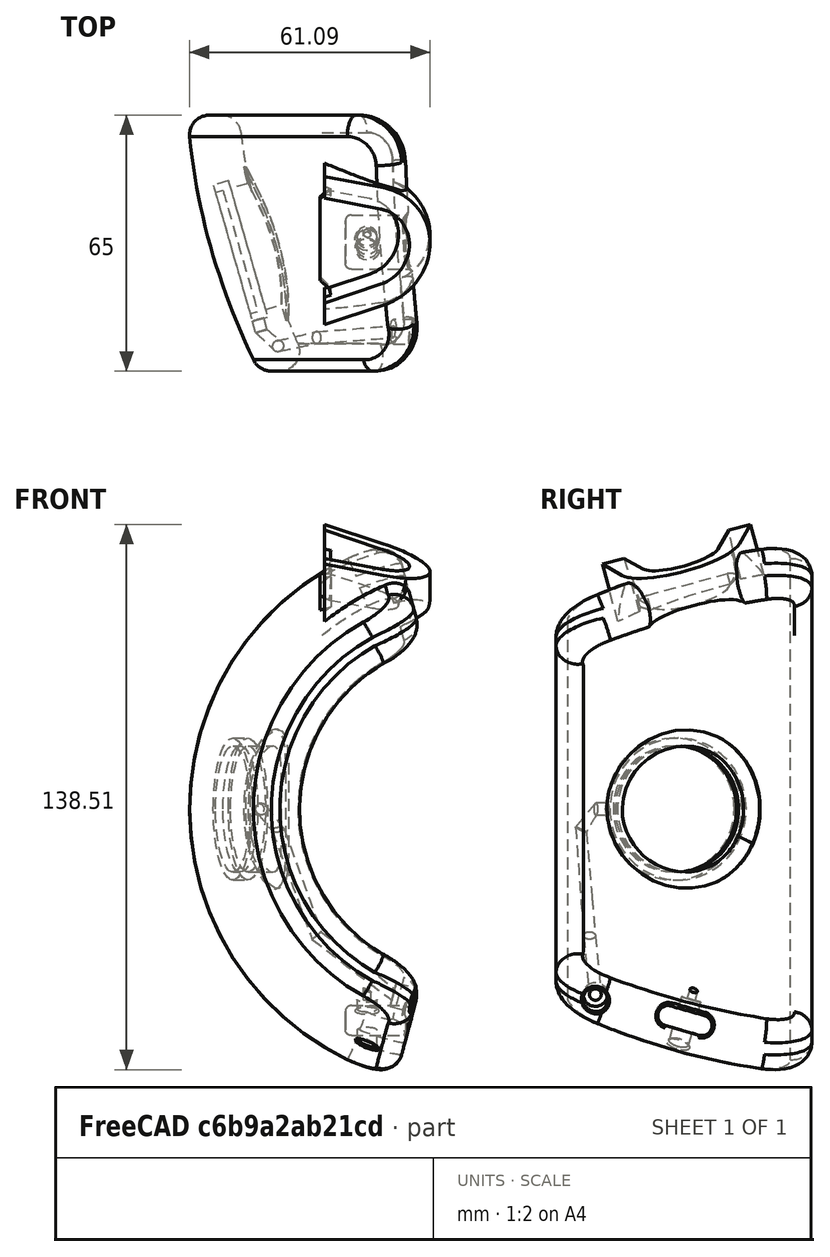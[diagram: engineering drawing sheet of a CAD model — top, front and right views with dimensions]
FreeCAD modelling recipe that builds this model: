
FCSTD DOCUMENT  (FreeCAD 0.17R13541 (Git))
Label: right_patch_foam_rubber_fastener_v6
License: All rights reserved
LicenseURL: http://en.wikipedia.org/wiki/All_rights_reserved
objects: Sketcher::SketchObject×22, PartDesign::Pocket×12, PartDesign::Plane×10, PartDesign::Fillet×5, PartDesign::Pad×3, PartDesign::Mirrored×3, PartDesign::Line×2, PartDesign::Chamfer×2, PartDesign::Revolution×1, PartDesign::SubtractivePipe×1, PartDesign::SubtractiveLoft×1, PartDesign::Groove×1, PartDesign::Body×1
note: 83 computed .brp shape members not serialized (recipe doc carries the construction recipe); baked Part::Feature solids carry a one-line shape summary decoded from their .brp

FEATURE [Sketcher::SketchObject] Sketch
  MapMode = 5
  Support = -> [XY_Plane]
  sketch-geometry (14):
    g0: LineSegment StartX=-53 StartY=0 StartZ=0 EndX=-40 EndY=0 EndZ=0
    g1: LineSegment StartX=-71 StartY=65 StartZ=0 EndX=-58 EndY=65 EndZ=0
    g2: Circle [constr] CenterX=-71 CenterY=65 CenterZ=0 NormalX=0 NormalY=0 NormalZ=1 AngleXU=0 Radius=1
    g3: Circle [constr] CenterX=-69 CenterY=32.5 CenterZ=0 NormalX=0 NormalY=0 NormalZ=1 AngleXU=0 Radius=1
    g4: Circle [constr] CenterX=-53 CenterY=0 CenterZ=0 NormalX=0 NormalY=0 NormalZ=1 AngleXU=0 Radius=1
    g5: BSplineCurve PolesCount=3 KnotsCount=2 Degree=2 IsPeriodic=0
    g6: GeomPoint [constr] X=-71 Y=65 Z=0
    g7: GeomPoint [constr] X=-53 Y=0 Z=0
    g8: Circle [constr] CenterX=-58 CenterY=65 CenterZ=0 NormalX=0 NormalY=0 NormalZ=1 AngleXU=0 Radius=1
    g9: Circle [constr] CenterX=-55 CenterY=32.5 CenterZ=0 NormalX=0 NormalY=0 NormalZ=1 AngleXU=0 Radius=1
    g10: Circle [constr] CenterX=-40 CenterY=0 CenterZ=0 NormalX=0 NormalY=0 NormalZ=1 AngleXU=0 Radius=1
    g11: BSplineCurve PolesCount=3 KnotsCount=2 Degree=2 IsPeriodic=0
    g12: GeomPoint [constr] X=-58 Y=65 Z=0
    g13: GeomPoint [constr] X=-40 Y=0 Z=0
  constraints (32):
    c: Horizontal(g0)
    c: Horizontal(g1)
    c: Coincident(g2,g1)
    c: Radius(g2) = 1
    c: Equal(g2,g3)
    c: Equal(g2,g4)
    c: Coincident(g4,g0)
    c: InternalAlignment(g2,g5)
    c: InternalAlignment(g3,g5)
    c: InternalAlignment(g4,g5)
    c: InternalAlignment(g6,g5)
    c: InternalAlignment(g7,g5)
    c: Coincident(g8,g1)
    c: Radius(g8) = 1
    c: Equal(g8,g9)
    c: Equal(g8,g10)
    c: Coincident(g10,g0)
    c: InternalAlignment(g8,g11)
    c: InternalAlignment(g9,g11)
    c: InternalAlignment(g10,g11)
    c: InternalAlignment(g12,g11)
    c: InternalAlignment(g13,g11)
    c: DistanceX(g1,g1) = 13  'upper thickness'
    c: DistanceX(g0,g0) = 13  'lower thickness'
    c: DistanceY(g0,g1) = 65
    c: DistanceY(g0,g-1) = 0
    c: DistanceY(g0,g9) = 32.5
    c: DistanceY(g0,g3) = 32.5
    c: DistanceX(g0,g-1) = 40  'lower radius'
    c: DistanceX(g3,g9) = 14  'middle thickness'
    c: DistanceX(g9,g0) = 15  'middle radius difference'
    c: DistanceX(g1,g0) = 18  'upper radius difference'
FEATURE [PartDesign::Revolution] Revolution
  Angle = 150
  Axis = (0,1,0)
  Base = (0,0,0)
  Midplane = true
  Profile = -> Sketch
  ReferenceAxis = -> Sketch [V_Axis]
FEATURE [PartDesign::Line] DatumLine
  AttacherType = Attacher::AttachEngineLine
  AttachmentOffset = pos=(47,0,0) rot=(0,1,0;0.279253rad)
  MapMode = 29
  Placement = pos=(0,47,0) rot=(0.470251,0.624045,0.624045;2.26246rad)
  Support = -> [X_Axis]
FEATURE [PartDesign::Plane] DatumPlane001
  AttachmentOffset = pos=(0,0,-45) rot=(0,0,1;0rad)
  MapMode = 2
  Placement = pos=(-43.2568,34.5963,0) rot=(0.470251,0.624045,0.624045;2.26246rad)
  Support = -> [DatumLine]
FEATURE [Sketcher::SketchObject] Sketch017
  MapMode = 5
  Placement = pos=(-43.2568,34.5963,0) rot=(0.470251,0.624045,0.624045;2.26246rad)
  Support = -> [DatumPlane001]
  sketch-geometry (1):
    g0: Circle CenterX=0 CenterY=0 CenterZ=0 NormalX=0 NormalY=0 NormalZ=1 AngleXU=0 Radius=19
  constraints (2):
    c: Coincident(g0,g-1)
    c: Radius(g0) = 19
FEATURE [PartDesign::Pad] Pad001
  BaseFeature = -> Revolution
  Length = 20
  Length2 = 100
  Profile = -> Sketch017
  Type = 3
  UpToFace = -> Revolution [Face3]
FEATURE [Sketcher::SketchObject] Sketch018
  ExternalGeometry = -> [DatumLine]
  MapMode = 5
  Support = -> [XY_Plane]
  sketch-geometry (8):
    g0: LineSegment [constr] StartX=-50.16 StartY=32.6169 StartZ=0 EndX=-44.5921 EndY=13.1994 EndZ=0
    g1: LineSegment StartX=-44.5921 StartY=13.1994 StartZ=0 EndX=-46.034 EndY=12.7859 EndZ=0
    g2: LineSegment StartX=-46.034 StartY=12.7859 StartZ=0 EndX=-50.1686 EndY=27.2048 EndZ=0
    g3: LineSegment StartX=-50.1686 StartY=27.2048 StartZ=0 EndX=-51.1298 EndY=26.9292 EndZ=0
    g4: LineSegment StartX=-51.1298 StartY=26.9292 StartZ=0 EndX=-51.6271 EndY=28.6634 EndZ=0
    g5: LineSegment StartX=-51.6271 StartY=28.6634 StartZ=0 EndX=-41.0277 EndY=31.7028 EndZ=0
    g6: LineSegment StartX=-41.0277 StartY=31.7028 StartZ=0 EndX=-36.3958 EndY=15.5496 EndZ=0
    g7: LineSegment StartX=-36.3958 StartY=15.5496 StartZ=0 EndX=-44.5921 EndY=13.1994 EndZ=0
  constraints (22):
    c: PointOnObject(g0,g-3)
    c: Perpendicular(g-3,g0)
    c: Distance(g0) = 20.2
    c: Coincident(g0,g1)
    c: Coincident(g1,g2)
    c: Coincident(g2,g3)
    c: Coincident(g3,g4)
    c: Coincident(g4,g5)
    c: Coincident(g5,g6)
    c: Coincident(g6,g7)
    c: Coincident(g7,g1)
    c: Perpendicular(g0,g1)
    c: Perpendicular(g0,g3)
    c: Perpendicular(g0,g5)
    c: Perpendicular(g0,g7)
    c: Parallel(g6,g0)
    c: Parallel(g2,g0)
    c: Parallel(g4,g0)
    c: Distance(g1) = 1.5
    c: Distance(g2) = 15
    c: Distance(g3) = 1
    c: DistanceX(g0) = -50.16
FEATURE [PartDesign::SubtractivePipe] SubtractivePipe
  AuxilleryCurvelinear = true
  AuxillerySpineTangent = false
  BaseFeature = -> Pad001
  Binormal = (0,0,0)
  Mode = 0
  Profile = -> Sketch018
  Refine = true
  Spine = -> Pad001 [Edge13,Edge14]
  SpineTangent = false
  Transformation = 0
  Transition = 0
FEATURE [Sketcher::SketchObject] Sketch019
  MapMode = 5
  Placement = pos=(-43.2568,34.5963,0) rot=(0.470251,0.624045,0.624045;2.26246rad)
  Support = -> [DatumPlane001]
  sketch-geometry (1):
    g0: Circle CenterX=0 CenterY=0 CenterZ=0 NormalX=0 NormalY=0 NormalZ=1 AngleXU=0 Radius=16
  constraints (2):
    c: Coincident(g0,g-1)
    c: Radius(g0) = 16
FEATURE [PartDesign::Pocket] Pocket007
  BaseFeature = -> SubtractivePipe
  Length = 30
  Length2 = 100
  Midplane = true
  Profile = -> Sketch019
  Type = 0
FEATURE [Sketcher::SketchObject] Sketch020
  ExternalGeometry = -> [DatumLine]
  MapMode = 5
  Placement = pos=(-45.2226,-12.9674,0) rot=(0.470251,0.624045,0.624045;2.26246rad)
  Support = -> [Pocket007]
  sketch-geometry (2):
    g0: Circle CenterX=45.1793 CenterY=0 CenterZ=0 NormalX=0 NormalY=0 NormalZ=1 AngleXU=0 Radius=16
    g1: Circle CenterX=45.1793 CenterY=0 CenterZ=0 NormalX=0 NormalY=0 NormalZ=1 AngleXU=0 Radius=18
  constraints (4):
    c: Coincident(g0,g-3)
    c: Coincident(g1,g0)
    c: Radius(g0) = 16
    c: Radius(g1) = 18
FEATURE [PartDesign::Pocket] Pocket008
  BaseFeature = -> Pocket007
  Length = 2
  Length2 = 2
  Profile = -> Sketch020
  Type = 4
FEATURE [PartDesign::Plane] DatumPlane
  AttachmentOffset = pos=(0,0,-9) rot=(0,0,1;0rad)
  MapMode = 5
  Placement = pos=(-9,1e-12,-1e-12) rot=(0.57735,0.57735,0.57735;2.0944rad)
  Support = -> [YZ_Plane]
FEATURE [Sketcher::SketchObject] Sketch003
  MapMode = 5
  Placement = pos=(-9,1e-12,-1e-12) rot=(0.57735,0.57735,0.57735;2.0944rad)
  Support = -> [DatumPlane]
  sketch-geometry (4):
    g0: ArcOfCircle CenterX=28.43 CenterY=52.5 CenterZ=0 NormalX=0 NormalY=0 NormalZ=1 AngleXU=0 Radius=2.575 StartAngle=1.85005 EndAngle=4.99164
    g1: ArcOfCircle CenterX=37.0814 CenterY=54.9807 CenterZ=0 NormalX=0 NormalY=0 NormalZ=1 AngleXU=0 Radius=2.575 StartAngle=4.99164 EndAngle=8.13323
    g2: LineSegment StartX=29.1398 StartY=50.0248 StartZ=0 EndX=37.7911 EndY=52.5055 EndZ=0
    g3: LineSegment StartX=27.7202 StartY=54.9752 StartZ=0 EndX=36.3716 EndY=57.456 EndZ=0
  constraints (10):
    c: Tangent(g0,g3) = 1.5708
    c: Tangent(g0,g2) = -1.5708
    c: Tangent(g2,g1) = -1.5708
    c: Tangent(g3,g1) = 1.5708
    c: Angle(g3,g-1) = -0.279253
    c: Distance(g0,g1) = 9
    c: Distance(g1,g1) = 5.15
    c: Parallel(g3,g2)
    c: DistanceX(g0) = 28.43
    c: DistanceY(g-1,g0) = 52.5
FEATURE [PartDesign::Plane] DatumPlane002
  AttachmentOffset = pos=(0,0,-18) rot=(0,0,1;0rad)
  MapMode = 4
  Placement = pos=(4.96147,29.6973,0) rot=(-0.515639,-0.684276,-0.515639;1.9414rad)
  Support = -> [DatumLine]
FEATURE [Sketcher::SketchObject] Sketch027
  MapMode = 5
  Placement = pos=(4.96147,29.6973,0) rot=(-0.515639,-0.684276,-0.515639;1.9414rad)
  Support = -> [DatumPlane002]
  sketch-geometry (1):
    g0: Circle CenterX=0 CenterY=-60.4737 CenterZ=0 NormalX=0 NormalY=0 NormalZ=1 AngleXU=0 Radius=1.5
  constraints (2):
    c: PointOnObject(g0,g-2)
    c: Radius(g0) = 1.5
FEATURE [PartDesign::Plane] DatumPlane003
  AttachmentOffset = pos=(0,0,0) rot=(0,-1,0;0.698132rad)
  MapMode = 5
  Placement = pos=(0,0,0) rot=(0,-1,0;0.698132rad)
  Support = -> [XY_Plane]
FEATURE [Sketcher::SketchObject] Sketch028
  MapMode = 5
  Placement = pos=(0,0,0) rot=(0,-1,0;0.698132rad)
  Support = -> [DatumPlane003]
  sketch-geometry (1):
    g0: Circle CenterX=-50 CenterY=8.5 CenterZ=0 NormalX=0 NormalY=0 NormalZ=1 AngleXU=0 Radius=1.5
  constraints (3):
    c: Radius(g0) = 1.5
    c: DistanceY(g-1,g0) = 8.5
    c: DistanceX(g0,g-1) = 50
FEATURE [PartDesign::Plane] DatumPlane004
  AttachmentOffset = pos=(0,0,4.5) rot=(-0.95157,-0.300144,-0.06654;0.457789rad)
  MapMode = 5
  Placement = pos=(0,0,4.5) rot=(-0.95157,-0.300144,-0.06654;0.457789rad)
  Support = -> [XY_Plane]
FEATURE [Sketcher::SketchObject] Sketch030
  MapMode = 5
  Placement = pos=(0,0,4.5) rot=(-0.95157,-0.300144,-0.06654;0.457789rad)
  Support = -> [DatumPlane004]
  sketch-geometry (1):
    g0: Circle CenterX=-49 CenterY=7 CenterZ=0 NormalX=0 NormalY=0 NormalZ=1 AngleXU=0 Radius=1.5
  constraints (3):
    c: Radius(g0) = 1.5
    c: DistanceY(g-1,g0) = 7
    c: DistanceX(g0,g-1) = 49
FEATURE [PartDesign::Fillet] Fillet020
  Base = -> Pocket008 [Edge7,Edge6,Edge9,Edge10]
  BaseFeature = -> Pocket008
  Radius = 12
FEATURE [PartDesign::Fillet] Fillet  label="Vorderkannte innen"
  Base = -> Fillet020 [Edge11,Edge1]
  BaseFeature = -> Fillet020
  Radius = 5
FEATURE [PartDesign::Pocket] Pocket  label="Kabelzug"
  BaseFeature = -> Fillet
  Length = 16
  Length2 = 100
  Profile = -> Sketch003
  Type = 0
FEATURE [Sketcher::SketchObject] Sketch022
  ExternalGeometry = -> [Pocket]
  MapMode = 5
  Placement = pos=(-6e-12,-11.0406,38.5032) rot=(1,0,0;0.279253rad)
  Support = -> [Pocket]
  sketch-geometry (1):
    g0: Circle CenterX=-19.5 CenterY=46.2996 CenterZ=0 NormalX=0 NormalY=0 NormalZ=1 AngleXU=0 Radius=2.55
  constraints (3):
    c: Radius(g0) = 2.55
    c: DistanceX(g-3,g0) = 5.5
    c: DistanceY(g0,g-3) = 4.5
FEATURE [PartDesign::Pocket] Pocket010  label="Bolzen"
  BaseFeature = -> Pocket
  Length = 3
  Length2 = 15
  Profile = -> Sketch022
  Refine = true
  Type = 4
FEATURE [Sketcher::SketchObject] Sketch023
  ExternalGeometry = -> [Pocket010]
  MapMode = 5
  Placement = pos=(-5e-12,-10.2137,35.6194) rot=(1,0,0;0.279253rad)
  Support = -> [Pocket010]
  sketch-geometry (1):
    g0: Circle CenterX=-25.5 CenterY=46.2996 CenterZ=0 NormalX=0 NormalY=0 NormalZ=1 AngleXU=0 Radius=1
  constraints (2):
    c: Coincident(g0,g-3)
    c: Radius(g0) = 1
FEATURE [PartDesign::Pocket] Pocket011  label="Bolzen demontage"
  BaseFeature = -> Pocket010
  Length = 5
  Length2 = 100
  Profile = -> Sketch023
  Type = 2
FEATURE [PartDesign::Mirrored] Mirrored
  BaseFeature = -> Pocket011
  MirrorPlane = -> XY_Plane
  Originals = -> [Pocket]
FEATURE [PartDesign::Mirrored] Mirrored004
  BaseFeature = -> Mirrored
  MirrorPlane = -> XY_Plane
  Originals = -> [Pocket010]
FEATURE [PartDesign::Mirrored] Mirrored005
  BaseFeature = -> Mirrored004
  MirrorPlane = -> XY_Plane
  Originals = -> [Pocket011]
FEATURE [Sketcher::SketchObject] Sketch025
  MapMode = 5
  Placement = pos=(0,0,0) rot=(0.621515,0.621515,0.476905;2.25159rad)
  Support = -> [Mirrored005]
  sketch-geometry (1):
    g0: Circle CenterX=10 CenterY=-50.4 CenterZ=0 NormalX=0 NormalY=0 NormalZ=1 AngleXU=0 Radius=3.1
  constraints (3):
    c: Radius(g0) = 3.1
    c: DistanceX(g0) = 10
    c: DistanceY(g0) = -50.4
FEATURE [PartDesign::Pocket] Pocket012
  BaseFeature = -> Mirrored005
  Length = 6
  Length2 = 100
  Profile = -> Sketch025
  Type = 0
FEATURE [PartDesign::Pocket] Pocket013
  BaseFeature = -> Pocket012
  Length = 3
  Length2 = 0.5
  Profile = -> Sketch027
  Type = 4
FEATURE [Sketcher::SketchObject] Sketch029
  ExternalGeometry = -> [Pocket013]
  MapMode = 5
  Placement = pos=(-5e-12,-10.2137,-35.6194) rot=(1,0,0;2.86234rad)
  Support = -> [Pocket013]
  sketch-geometry (1):
    g0: Circle CenterX=47.5188 CenterY=0 CenterZ=0 NormalX=0 NormalY=0 NormalZ=1 AngleXU=0 Radius=1.5
  constraints (2):
    c: Coincident(g0,g-3)
    c: Radius(g0) = 1.5
FEATURE [PartDesign::Chamfer] Chamfer  label="Vacuum connector"
  Base = -> Pocket [Edge11,Edge20]
  BaseFeature = -> Pocket
  Size = 0.5
FEATURE [PartDesign::Fillet] Fillet016  label="Bowden end face"
  Base = -> Chamfer [Face50,Face38]
  BaseFeature = -> Chamfer
  Radius = 1.5
FEATURE [PartDesign::Fillet] Fillet017  label="Bowden front edge"
  Base = -> Fillet016 [Edge94,Edge3]
  BaseFeature = -> Fillet016
  Radius = 0.5
FEATURE [PartDesign::Chamfer] Chamfer001  label="Bolt edges"
  Base = -> Fillet017 [Edge188,Edge93,Edge9,Edge49]
  BaseFeature = -> Fillet017
  Size = 0.5
FEATURE [Sketcher::SketchObject] Sketch031  label="Sketch032"
  ExternalGeometry = -> [Pocket013]
  MapMode = 5
  Placement = pos=(-5.79555,0,1.55291) rot=(0.621515,0.621515,0.476905;2.25159rad)
  Support = -> [Pocket013]
  sketch-geometry (1):
    g0: Circle CenterX=10 CenterY=-50.4 CenterZ=0 NormalX=0 NormalY=0 NormalZ=1 AngleXU=0 Radius=1.5
  constraints (2):
    c: Coincident(g0,g-3)
    c: Radius(g0) = 1.5
FEATURE [PartDesign::SubtractiveLoft] SubtractiveLoft
  BaseFeature = -> Pocket013
  Closed = false
  Profile = -> Sketch029
  Refine = true
  Ruled = true
  Sections = -> [Sketch030,Sketch028,Sketch031]
FEATURE [PartDesign::Plane] DatumPlane005
  AttachmentOffset = pos=(0,0,0) rot=(0,1,0;0.994838rad)
  MapMode = 5
  Placement = pos=(0,0,0) rot=(0,1,0;0.994838rad)
  Support = -> [XY_Plane]
FEATURE [Sketcher::SketchObject] Sketch032  label="Sketch033"
  MapMode = 5
  Placement = pos=(0,0,0) rot=(0,1,0;0.994838rad)
  Support = -> [DatumPlane005]
  sketch-geometry (4):
    g0: LineSegment StartX=-70 StartY=40.5 StartZ=0 EndX=-40 EndY=40.5 EndZ=0
    g1: LineSegment StartX=-40 StartY=40.5 StartZ=0 EndX=-40 EndY=24.5 EndZ=0
    g2: LineSegment StartX=-40 StartY=24.5 StartZ=0 EndX=-70 EndY=24.5 EndZ=0
    g3: LineSegment StartX=-70 StartY=24.5 StartZ=0 EndX=-70 EndY=40.5 EndZ=0
  constraints (12):
    c: Coincident(g0,g1)
    c: Coincident(g1,g2)
    c: Coincident(g2,g3)
    c: Coincident(g3,g0)
    c: Horizontal(g0)
    c: Horizontal(g2)
    c: Vertical(g1)
    c: Vertical(g3)
    c: DistanceY(g3,g3) = 16
    c: DistanceY(g-1,g2) = 24.5
    c: DistanceX(g1) = -40
    c: DistanceX(g0,g0) = 30
FEATURE [PartDesign::Line] DatumLine001
  AttacherType = Attacher::AttachEngineLine
  MapMode = 31
  Placement = pos=(-25.5,31.152,0) rot=(0,0,1;0rad)
  Support = -> [XY_Plane]
FEATURE [PartDesign::Pocket] Pocket014
  BaseFeature = -> Chamfer001
  Length = 5
  Length2 = 100
  Profile = -> Sketch032
  Refine = true
  Reversed = true
  Type = 1
FEATURE [PartDesign::Plane] DatumPlane006
  AttachmentOffset = pos=(0,0,57) rot=(1,0,0;0.261799rad)
  MapMode = 5
  Placement = pos=(0,0,57) rot=(1,0,0;0.261799rad)
  Support = -> [XY_Plane]
FEATURE [Sketcher::SketchObject] Sketch033  label="Sketch034"
  ExternalGeometry = -> [DatumLine001]
  MapMode = 5
  Placement = pos=(0,0,57) rot=(1,0,0;0.261799rad)
  Support = -> [DatumPlane006]
  sketch-geometry (2):
    g0: ArcOfCircle CenterX=-25.5 CenterY=32.21 CenterZ=0 NormalX=0 NormalY=0 NormalZ=1 AngleXU=0 Radius=16 StartAngle=3.86433 EndAngle=8.70204
    g1: LineSegment StartX=-37.5 StartY=21.627 StartZ=0 EndX=-37.5 EndY=42.793 EndZ=0
  constraints (7):
    c: Radius(g0) = 16
    c: DistanceX(g0) = -25.5
    c: DistanceY(g0) = 32.21
    c: Vertical(g1)
    c: Coincident(g0,g1)
    c: Coincident(g0,g1)
    c: DistanceX(g0,g0) = 12
FEATURE [PartDesign::Pad] Pad
  BaseFeature = -> Pocket014
  Length = 5
  Length2 = 21.8
  Profile = -> Sketch033
  Refine = true
  Reversed = true
  Type = 4
FEATURE [PartDesign::Plane] DatumPlane007
  MapMode = 11
  Placement = pos=(-18.84,10,-47.1297) rot=(0.650394,-0.572645,0.499065;3.96961rad)
  Support = -> [Pad]
FEATURE [Sketcher::SketchObject] Sketch036  label="Sketch037"
  ExternalGeometry = -> [Pad]
  MapMode = 5
  Placement = pos=(0,0,57) rot=(1,0,0;0.261799rad)
  Support = -> [DatumPlane006]
  sketch-geometry (8):
    g0: LineSegment StartX=-21.3589 StartY=47.6648 StartZ=0 EndX=-36.3589 EndY=51.684 EndZ=0
    g1: LineSegment StartX=-36.3589 StartY=12.736 StartZ=0 EndX=-21.3589 EndY=16.7552 EndZ=0
    g2: LineSegment StartX=-21.3589 StartY=47.6648 StartZ=0 EndX=-21.3589 EndY=16.7552 EndZ=0
    g3: LineSegment StartX=-36.3589 StartY=51.684 StartZ=0 EndX=-36.3589 EndY=45.7312 EndZ=0
    g4: LineSegment StartX=-36.3589 StartY=45.7312 StartZ=0 EndX=-22.3589 EndY=41.9799 EndZ=0
    g5: LineSegment StartX=-22.3589 StartY=41.9799 StartZ=0 EndX=-22.3589 EndY=22.4401 EndZ=0
    g6: LineSegment StartX=-22.3589 StartY=22.4401 StartZ=0 EndX=-36.3589 EndY=18.6888 EndZ=0
    g7: LineSegment StartX=-36.3589 StartY=18.6888 StartZ=0 EndX=-36.3589 EndY=12.736 EndZ=0
  constraints (24):
    c: Coincident(g2,g0)
    c: Coincident(g2,g1)
    c: Vertical(g2)
    c: Angle(g0,g2) = 1.8326
    c: Coincident(g0,g3)
    c: Vertical(g3)
    c: Coincident(g3,g4)
    c: Coincident(g4,g5)
    c: Vertical(g5)
    c: Coincident(g5,g6)
    c: Coincident(g6,g7)
    c: Coincident(g7,g1)
    c: Vertical(g7)
    c: Parallel(g4,g0)
    c: Parallel(g6,g1)
    c: DistanceX(g5,g1) = 1
    c: DistanceX(g0,g0) = 15
    c: DistanceX(g1,g1) = 15
    c: Tangent(g0,g-3)
    c: Tangent(g1,g-3)
    c: PointOnObject(g0,g-3)
    c: PointOnObject(g1,g-3)
    c: Distance(g-3,g4) = 10.25
    c: Distance(g-3,g6) = 10.25
FEATURE [PartDesign::Plane] DatumPlane008
  AttachmentOffset = pos=(0,0,0) rot=(0,1,0;0.872665rad)
  MapMode = 5
  Placement = pos=(0,0,0) rot=(0,1,0;0.872665rad)
  Support = -> [XY_Plane]
FEATURE [Sketcher::SketchObject] Sketch039  label="Sketch040"
  MapMode = 5
  Placement = pos=(0,0,0) rot=(0,1,0;0.872665rad)
  Support = -> [DatumPlane008]
  sketch-geometry (8):
    g0: Circle [constr] CenterX=-58 CenterY=65 CenterZ=0 NormalX=0 NormalY=0 NormalZ=1 AngleXU=0 Radius=6
    g1: Circle [constr] CenterX=-55 CenterY=32.5 CenterZ=0 NormalX=0 NormalY=0 NormalZ=1 AngleXU=0 Radius=6
    g2: Circle [constr] CenterX=-40 CenterY=0 CenterZ=0 NormalX=0 NormalY=0 NormalZ=1 AngleXU=0 Radius=6
    g3: BSplineCurve PolesCount=3 KnotsCount=2 Degree=2 IsPeriodic=0
    g4: GeomPoint [constr] X=-58 Y=65 Z=0
    g5: GeomPoint [constr] X=-40 Y=0 Z=0
    g6: LineSegment StartX=-58 StartY=65 StartZ=0 EndX=-40 EndY=65 EndZ=0
    g7: LineSegment StartX=-40 StartY=65 StartZ=0 EndX=-40 EndY=0 EndZ=0
  constraints (19):
    c: Radius(g0) = 6
    c: Equal(g0,g1)
    c: Equal(g0,g2)
    c: InternalAlignment(g0,g3)
    c: InternalAlignment(g1,g3)
    c: InternalAlignment(g2,g3)
    c: InternalAlignment(g4,g3)
    c: InternalAlignment(g5,g3)
    c: DistanceY(g-1,g2) = 0
    c: DistanceY(g-1,g1) = 32.5
    c: DistanceY(g-1,g0) = 65
    c: DistanceX(g2,g-1) = 40
    c: DistanceX(g1,g2) = 15
    c: DistanceX(g0,g2) = 18
    c: Coincident(g6,g0)
    c: Horizontal(g6)
    c: Coincident(g6,g7)
    c: Coincident(g7,g2)
    c: Vertical(g7)
FEATURE [PartDesign::Fillet] Fillet024
  Base = -> Pad [Edge110]
  BaseFeature = -> Pad
  Radius = 10
FEATURE [PartDesign::Pad] Pad003
  BaseFeature = -> Fillet024
  Length = 5
  Length2 = 13.3
  Profile = -> Sketch036
  Reversed = true
  Type = 4
FEATURE [Sketcher::SketchObject] Sketch041  label="Sketch042"
  MapMode = 5
  Placement = pos=(-9,1e-12,-1e-12) rot=(0.57735,0.57735,0.57735;2.0944rad)
  Support = -> [DatumPlane]
  sketch-geometry (5):
    g0: LineSegment StartX=26.2898 StartY=62.9836 StartZ=0 EndX=31.7998 EndY=53.4399 EndZ=0
    g1: LineSegment StartX=37.3979 StartY=54.9399 StartZ=0 EndX=37.3979 EndY=65.96 EndZ=0
    g2: LineSegment StartX=37.3979 StartY=65.96 StartZ=0 EndX=26.2898 EndY=62.9836 EndZ=0
    g3: LineSegment [constr] StartX=35.4 StartY=51.2 StartZ=0 EndX=31.8438 EndY=64.4718 EndZ=0
    g4: ArcOfCircle CenterX=34.3979 CenterY=54.9399 CenterZ=0 NormalX=0 NormalY=0 NormalZ=1 AngleXU=0 Radius=3 StartAngle=3.66519 EndAngle=6.28319
  constraints (15):
    c: Coincident(g1,g2)
    c: Coincident(g2,g0)
    c: PointOnObject(g3,g2)
    c: Perpendicular(g3,g2)
    c: Angle(g1,g3) = 0.261799
    c: Angle(g3,g0) = 0.261799
    c: Distance(g2) = 11.5
    c: DistanceX(g3) = 35.4
    c: DistanceY(g3) = 51.2
    c: Angle(g-2,g3) = 0.261799
    c: Tangent(g0,g4) = -1.5708
    c: Tangent(g1,g4) = -1.5708
    c: Distance(g3) = 13.74
    c: PointOnObject(g4,g3)
    c: Radius(g4) = 3
FEATURE [PartDesign::Plane] DatumPlane009
  AttachmentOffset = pos=(0,0,0) rot=(0,1,0;0.261799rad)
  MapMode = 5
  Placement = pos=(0,0,57) rot=(0.704063,0.704063,0.092692;0.36971rad)
  Support = -> [DatumPlane006]
FEATURE [Sketcher::SketchObject] Sketch037  label="Sketch038"
  ExternalGeometry = -> [Pad003]
  MapMode = 5
  Placement = pos=(0,0,57) rot=(0.704063,0.704063,0.092692;0.36971rad)
  Support = -> [DatumPlane009]
  sketch-geometry (4):
    g0: ArcOfCircle CenterX=-23.5084 CenterY=32.21 CenterZ=0 NormalX=0 NormalY=0 NormalZ=1 AngleXU=0 Radius=10.25 StartAngle=4.97419 EndAngle=7.59218
    g1: LineSegment StartX=-20.8555 StartY=42.1107 StartZ=0 EndX=-39.8862 EndY=47.21 EndZ=0
    g2: LineSegment StartX=-39.8862 StartY=47.21 StartZ=0 EndX=-39.8862 EndY=17.21 EndZ=0
    g3: LineSegment StartX=-39.8862 StartY=17.21 StartZ=0 EndX=-20.8555 EndY=22.3093 EndZ=0
  constraints (9):
    c: Coincident(g1,g2)
    c: Coincident(g2,g3)
    c: Radius(g0) = 10.25
    c: Tangent(g1,g0) = -1.5708
    c: Tangent(g3,g0) = -1.5708
    c: Vertical(g2)
    c: Angle(g2,g1) = 1.309
    c: Angle(g3,g2) = 1.309
    c: DistanceY(g2,g2) = 30
FEATURE [PartDesign::Pocket] Pocket015
  BaseFeature = -> Pad003
  Length = 18
  Length2 = 100
  Profile = -> Sketch037
  Type = 0
FEATURE [Sketcher::SketchObject] Sketch038  label="Sketch039"
  MapMode = 5
  Placement = pos=(0,0,57) rot=(0.704063,0.704063,0.092692;0.36971rad)
  Support = -> [DatumPlane009]
  sketch-geometry (4):
    g0: LineSegment StartX=-47.2876 StartY=55.9087 StartZ=0 EndX=-4.49882 EndY=55.9087 EndZ=0
    g1: LineSegment StartX=-4.49882 StartY=55.9087 StartZ=0 EndX=-4.49882 EndY=8.3403 EndZ=0
    g2: LineSegment StartX=-4.49882 StartY=8.3403 StartZ=0 EndX=-47.2876 EndY=8.3403 EndZ=0
    g3: LineSegment StartX=-47.2876 StartY=8.3403 StartZ=0 EndX=-47.2876 EndY=55.9087 EndZ=0
  constraints (8):
    c: Coincident(g0,g1)
    c: Coincident(g1,g2)
    c: Coincident(g2,g3)
    c: Coincident(g3,g0)
    c: Horizontal(g0)
    c: Horizontal(g2)
    c: Vertical(g1)
    c: Vertical(g3)
FEATURE [PartDesign::Pocket] Pocket016
  BaseFeature = -> Pocket015
  Length = 7.5
  Length2 = 100
  Profile = -> Sketch038
  Type = 4
FEATURE [PartDesign::Groove] Groove
  Angle = 50
  Axis = (0,1,0)
  Base = (0,0,0)
  BaseFeature = -> Pocket016
  Profile = -> Sketch039
  ReferenceAxis = -> Y_Axis
FEATURE [Sketcher::SketchObject] Sketch040  label="Sketch041"
  ExternalGeometry = -> [Groove]
  MapMode = 5
  Placement = pos=(0,0,57) rot=(0.704063,0.704063,0.092692;0.36971rad)
  Support = -> [DatumPlane009]
  sketch-geometry (1):
    g0: Circle CenterX=-23.5084 CenterY=32.21 CenterZ=0 NormalX=0 NormalY=0 NormalZ=1 AngleXU=0 Radius=5.25
  constraints (2):
    c: Radius(g0) = 5.25
    c: Coincident(g-3,g0)
FEATURE [PartDesign::Pocket] Pocket017
  BaseFeature = -> Groove
  Length = 23
  Length2 = 100
  Profile = -> Sketch040
  Type = 0
FEATURE [PartDesign::Pocket] Pocket018
  BaseFeature = -> Pocket017
  Length = 8.5
  Length2 = 100
  Profile = -> Sketch041
  Type = 0
FEATURE [PartDesign::Body] Body
  Group = -> [Sketch,Revolution,DatumLine,DatumPlane001,Sketch017,Pad001,Sketch018,SubtractivePipe,Sketch019,Pocket007,Sketch020,Pocket008,Sketch003,Fillet020,Fillet,DatumPlane,Pocket,Sketch022,Pocket010,Sketch023,Pocket011,Mirrored,Mirrored004,Mirrored005,Sketch025,Pocket012,DatumPlane002,Sketch027,Pocket013,DatumPlane003,Sketch028,Sketch029,DatumPlane004,Sketch030,Sketch031,SubtractiveLoft,Chamfer,+26 more]
  Origin = -> Origin
  Tip = -> Groove
